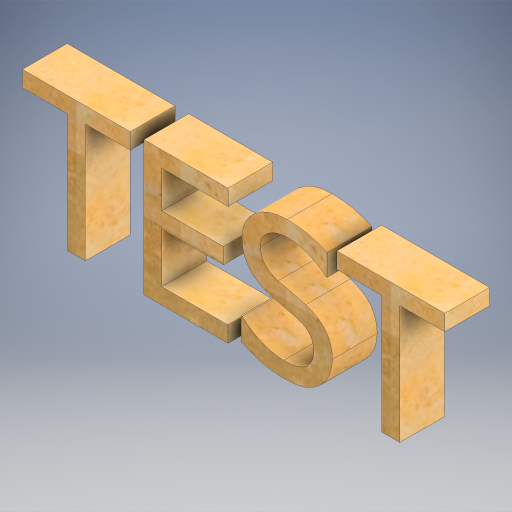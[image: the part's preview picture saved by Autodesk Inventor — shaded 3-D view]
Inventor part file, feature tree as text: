
AUTODESK INVENTOR PART (.ipt)
format: ipt  version: 2023.1 (Build 271208000, 208)  size: 482,816 bytes
history: native  units: in
note: dims shown in document units (in); Inventor stores cm internally (conversion verified against a paired STEP export)
features: extrude x1, sketch x1
ambient origin geometry x8: Origin, YZ Plane, XZ Plane, XY Plane, X Axis, Y Axis, Z Axis, Center Point
bodies: Solid1 (feature_tree)
feature tree (2):
  extrude  "Extrusion1"  [1 undecoded]
  sketch  "Sketch1"  dims[d0=1.0in d1=0.0in]
note: 1 required parameter value undecoded (feature->parameter linkage not recoverable at this tier; creation-order binding heuristic only, values carry confidence <= 0.55)
